# Revit family: 63_PHILIPS_ClearWay gen2_BGP307 Performer_3D
name_source: partatom
category: Lighting Fixtures
revit_build: Autodesk Revit 2016 (Build: 20150220_1215(x64)
units: mm (PartAtom-declared; Revit-internal decimal feet)

## family parameters
Always vertical = Yes
Cut with Voids When Loaded = No
Light Source = No
Part Type = Normal
Room Calculation Point = No
Round Connector Dimension = Use Diameter
Shared = No
Work Plane-Based = Yes

## types (1)
- No IES available
    Apparent Load = 0 VA
    Default Elevation = 0 mm  [stored 0 ft]
    Description = BGP307 Performer
    Lamp = LAMP NAME
    Light loss factor = 1
    Manufacturer = Philips
    Model = ClearWay Gen2
    Rotation Default = 90.00°
    Rotation XZ = 90.00°
    Type Comments = On Pole
    URL = http://www.lighting.philips.com
    height = 95 mm  [stored 0.31168 ft]
    height 01 = 0 mm  [stored 0 ft]
    length = 550.26 mm
    light source = 150 mm
    offset = 14 mm  [stored 0.0459318 ft]
    radius Pole = 45 mm  [stored 0.147638 ft]
    rim height = 2 mm  [stored 0.00656168 ft]
    width = 326 mm  [stored 1.06955 ft]

note: [stored X ft] marks values corroborated as IEEE doubles in the binary element streams (Revit-internal decimal feet)

## geometry (parser evidence)
native form markers: Blend x296, Sweep x1
no freeform markers — native parametric forms only
